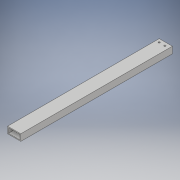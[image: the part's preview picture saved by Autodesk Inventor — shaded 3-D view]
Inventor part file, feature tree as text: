
AUTODESK INVENTOR PART (.ipt)
format: ipt  version: 2017 (Build 210142000, 142)  size: 117,760 bytes
history: native  units: in
note: dims shown in document units (in); Inventor stores cm internally (conversion verified against a paired STEP export)
features: sketch x2, extrude x1, hole x1
ambient origin geometry x8: Origin, YZ Plane, XZ Plane, XY Plane, X Axis, Y Axis, Z Axis, Center Point
bodies: Solid1 (feature_tree)
feature tree (4):
  extrude  "Extrusion1"  Depth=1.0in
  hole  "Hole1"  [1 undecoded]
  sketch  "Sketch1"  dims[d0=2.0in d1=1.0in]
  sketch  "Sketch2"  dims[d2=1.75in d3=0.75in d4=0.125in d5=0.125in d6=23.0in d7=0.0in d8=0.25in d9=90.0deg d10=0.5in d11=0.5in d12=12.25in d13=0.25in d14=0.75in d15=0.375in d16=0.25in d17=0.5635in d18=1.0in d19=0.8108in]
note: 1 required parameter value undecoded (feature->parameter linkage not recoverable at this tier; creation-order binding heuristic only, values carry confidence <= 0.55)
